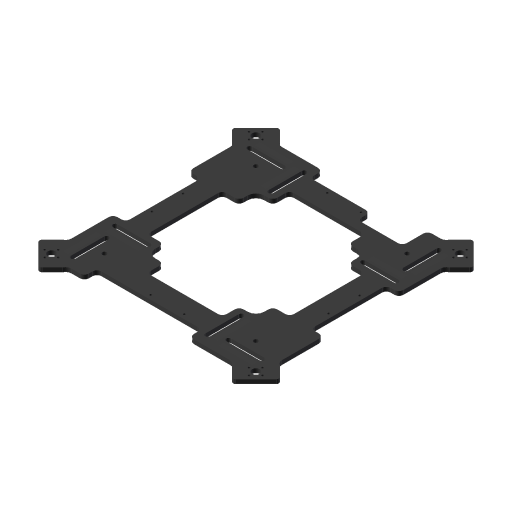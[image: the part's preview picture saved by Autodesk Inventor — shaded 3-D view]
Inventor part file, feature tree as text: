
AUTODESK INVENTOR PART (.ipt)
format: ipt  version: 2023 (Build 270158000, 158)  size: 1,358,848 bytes
history: native  units: mm
features: sketch x4, extrude x3, fillet x3, chamfer x1, mirror x1
ambient origin geometry x8: Origin, YZ Plane, XZ Plane, XY Plane, X Axis, Y Axis, Z Axis, Center Point
bodies: Solid1 (feature_tree)
feature tree (12):
  extrude  "Extrusion1"  Depth=3.0mm
  extrude  "Extrusion2"  Depth=10.0mm TaperAngle=0.0deg
  sketch  "Sketch4"  dims[d7=3.0mm]
  chamfer  "Chamfer1"  Distance=20.0mm
  fillet  "Fillet1"  Radius=10.0mm
  fillet  "Fillet2"  Radius=6.0mm
  extrude  "Extrusion3"  Depth=3.0mm
  fillet  "Fillet3"  Radius=7.0mm
  sketch  "Sketch2"  dims[d2=20.0mm d3=3.0mm]
  sketch  "Sketch3"  dims[d4=20.0mm d5=10.0mm d6=0.0mm]
  sketch  "Sketch5"  dims[d8=18.5mm d9=20.0mm d10=10.0mm d11=0.0mm d12=6.0mm d13=2.0mm d14=45.0deg d15=3.0mm d16=7.0mm d17=125.0mm d18=15.0mm d19=15.0mm d20=90.0mm d21=15.0mm d22=15.0mm d23=125.0mm d24=12.0mm d25=12.0mm d26=10.0mm d27=0.0mm d28=5.0mm]
  mirror  "Mirror7"
